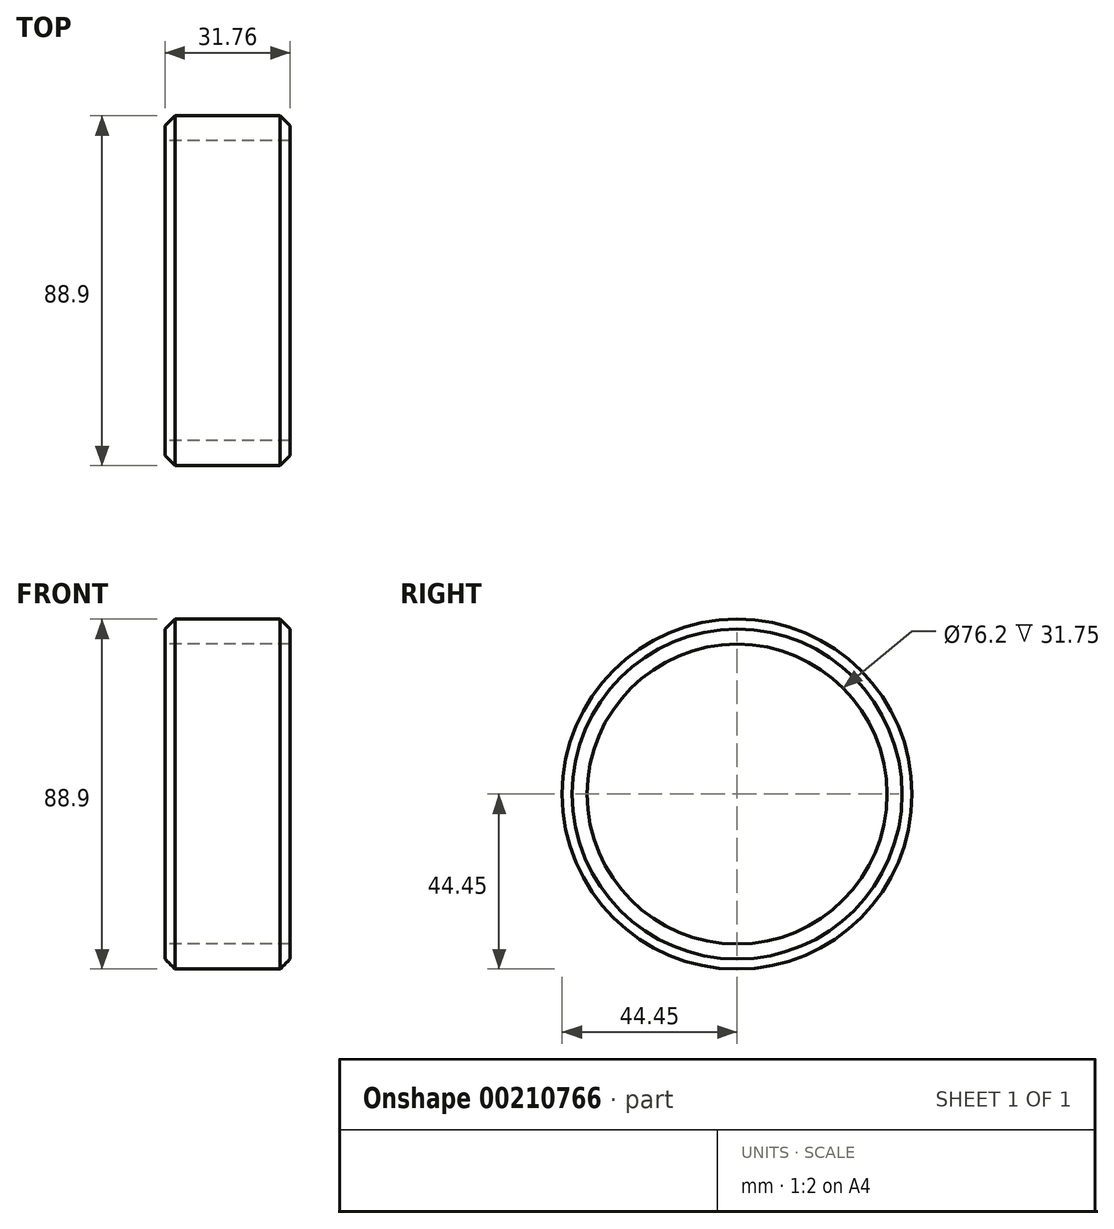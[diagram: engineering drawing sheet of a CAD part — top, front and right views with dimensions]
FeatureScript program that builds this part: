
annotation { "Feature Type Name" : "Feature", "Feature Type Description" : "" }
export const myFeature = defineFeature(function(context is Context, id is Id, definition is map)
    precondition{}
    {
        {
            var Q0;
            Q0=qCreatedBy(makeId("Right.planeOp"),FACE);
            var sketch = newSketch(context, id + "F0", { "sketchPlane" : qUnion([Q0])});
            skCircle(sketch, "E0", {"center": v(0, 0) * mm, "radius": 38.1 * mm});
            skCircle(sketch, "E1", {"center": v(0, 0) * mm, "radius": 44.45 * mm});
            skSolve(sketch);
        }
        {
            var Q0;
            Q0 = qSketchRegion(id + "F0", true);
            extrude(context, id + "F1", {"entities" : qUnion([Q0]), "endBound" : BoundingType.SYMMETRIC, "depth" : 31.75 * mm});
        }
        {
            var Q0;
            Q0=makeQuery(id+"F1.opExtrude","CAP_EDGE",EDGE,{"disambiguationData":[OSD([sQuery(id+"F0.wireOp",EDGE,"E1")])],"isStart":false});
            var Q1;
            Q1=makeQuery(id+"F1.opExtrude","CAP_EDGE",EDGE,{"disambiguationData":[OSD([sQuery(id+"F0.wireOp",EDGE,"E1")])],"isStart":true});
            chamfer(context, id + "F2", {"entities" : qUnion([Q0, Q1]), "width" : 2.54 * mm});
        }
    });
